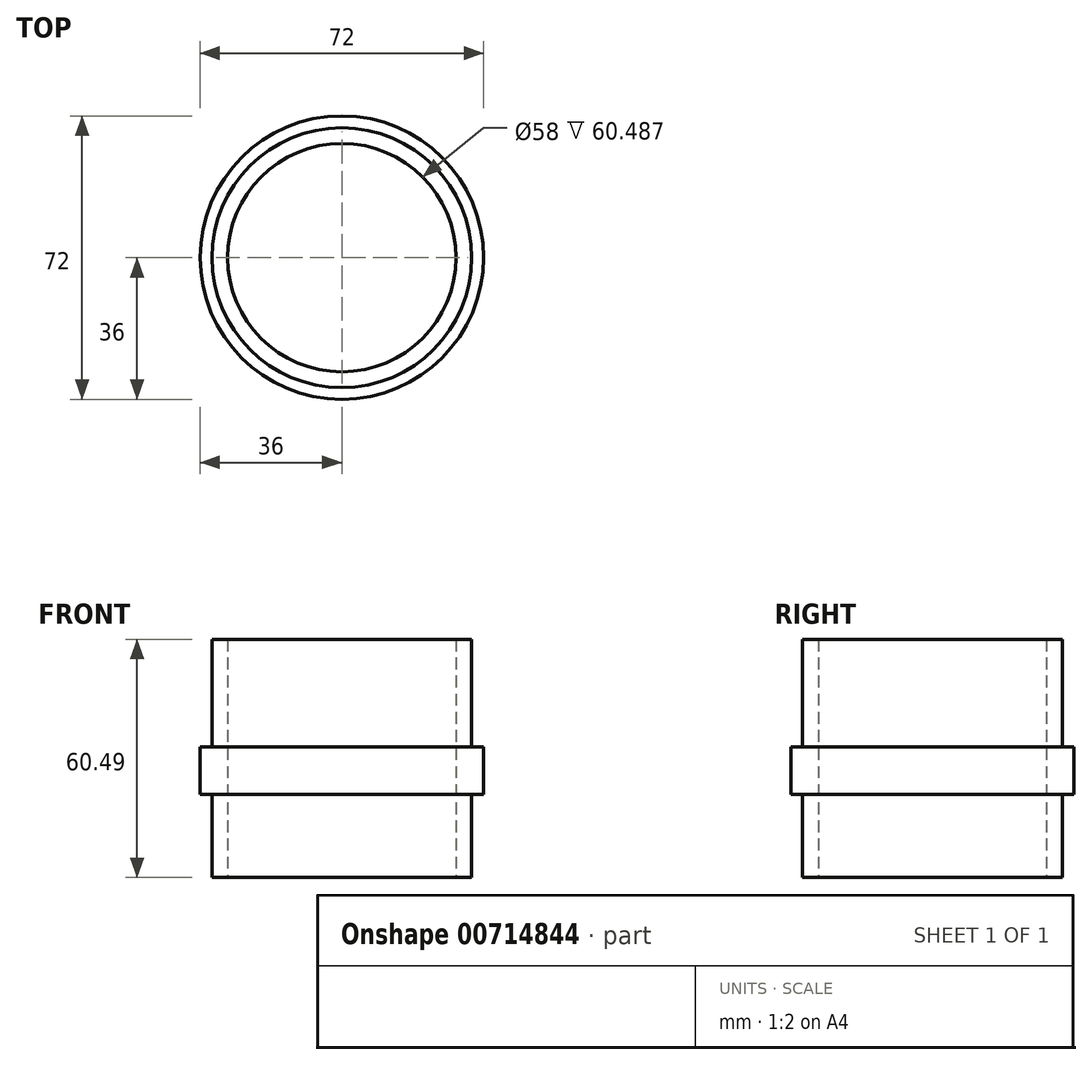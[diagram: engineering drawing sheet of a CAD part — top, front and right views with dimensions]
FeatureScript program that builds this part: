
annotation { "Feature Type Name" : "Feature", "Feature Type Description" : "" }
export const myFeature = defineFeature(function(context is Context, id is Id, definition is map)
    precondition{}
    {
        {
            var Q0;
            Q0=qCreatedBy(makeId("Front.planeOp"),FACE);
            var sketch = newSketch(context, id + "F0", { "sketchPlane" : qUnion([Q0])});
            skLineSegment(sketch, "E0", {"start": v(29, 0) * mm, "end": v(29, 60.49) * mm});
            skLineSegment(sketch, "E1", {"start": v(29, 60.49) * mm, "end": v(33, 60.49) * mm});
            skLineSegment(sketch, "E2", {"start": v(33, 60.49) * mm, "end": v(33, 33.14) * mm});
            skLineSegment(sketch, "E3", {"start": v(33, 33.14) * mm, "end": v(36, 33.14) * mm});
            skLineSegment(sketch, "E4", {"start": v(36, 33.14) * mm, "end": v(36, 21.14) * mm});
            skLineSegment(sketch, "E5", {"start": v(36, 21.14) * mm, "end": v(33, 21.14) * mm});
            skLineSegment(sketch, "E6", {"start": v(33, 21.14) * mm, "end": v(33, 0) * mm});
            skLineSegment(sketch, "E7", {"start": v(33, 0) * mm, "end": v(29, 0) * mm});
            skLineSegment(sketch, "E8", {"start": v(0, 0) * mm, "end": v(0, 29.73) * mm, "construction": true});
            skSolve(sketch);
        }
        {
            var Q0;
            Q0=makeQuery(id+"F0.imprint","IMPRINT",FACE,{"disambiguationData":[TD([[makeQuery(id+"F0.imprint","IMPRINT",EDGE,{"derivedFrom":sQuery(id+"F0.wireOp",EDGE,"E0")}),-1.0]])]});
            var Q1;
            Q1=sQuery(id+"F0.wireOp",EDGE,"E8");
            revolve(context, id + "F1", {"surfaceOperationType" : NewSurfaceOperationType.NEW, "entities" : qUnion([Q0]), "axis" : qUnion([Q1]), "revolveType" : RevolveType.FULL});
        }
    });
